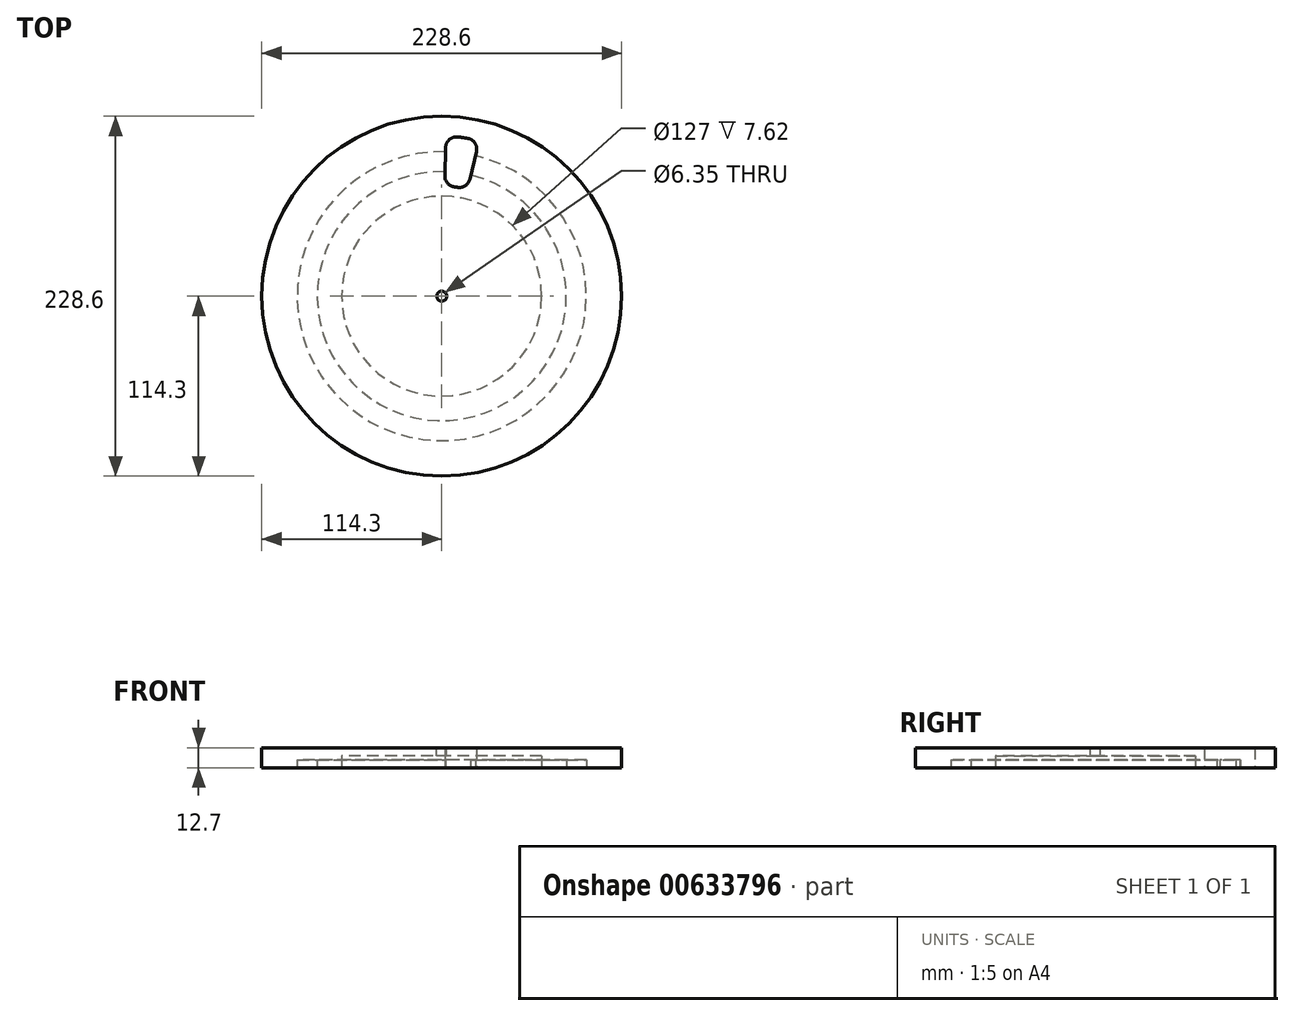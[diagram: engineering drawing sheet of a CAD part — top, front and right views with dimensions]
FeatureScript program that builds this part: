
annotation { "Feature Type Name" : "Feature", "Feature Type Description" : "" }
export const myFeature = defineFeature(function(context is Context, id is Id, definition is map)
    precondition{}
    {
        {
            var Q0;
            Q0=qCreatedBy(makeId("Top.planeOp"),FACE);
            var sketch = newSketch(context, id + "F0", { "sketchPlane" : qUnion([Q0])});
            skCircle(sketch, "E0", {"center": v(0, 0) * mm, "radius": 114.3 * mm});
            skSolve(sketch);
        }
        {
            var Q0;
            Q0 = qSketchRegion(id + "F0", true);
            extrude(context, id + "F1", {"entities" : qUnion([Q0]), "depth" : 12.7 * mm, "offsetDistance" : 25.4 * mm});
        }
        {
            var Q0;
            Q0=qCreatedBy(makeId("Top.planeOp"),FACE);
            var sketch = newSketch(context, id + "F2", { "sketchPlane" : qUnion([Q0])});
            skCircle(sketch, "E1", {"center": v(0, 0) * mm, "radius": 63.5 * mm});
            skSolve(sketch);
        }
        {
            var Q0;
            Q0 = qSketchRegion(id + "F2", true);
            var Q1;
            Q1=makeQuery(id+"F1.opExtrude","CAP_FACE",FACE,{"disambiguationData":[OSD([sQuery(id+"F0.wireOp",EDGE,"E0")])],"isStart":false});
            extrude(context, id + "F3", {"entities" : qUnion([Q0]), "operationType" : NewBodyOperationType.REMOVE, "endBound" : BoundingType.UP_TO_SURFACE, "depth" : 20.32 * mm, "endBoundEntityFace" : qUnion([Q1]), "hasOffset" : true, "offsetDistance" : 5.08 * mm});
        }
        {
            var Q0;
            Q0=makeQuery(id+"F1.opExtrude","CAP_FACE",FACE,{"disambiguationData":[OSD([sQuery(id+"F0.wireOp",EDGE,"E0")])],"isStart":true});
            var sketch = newSketch(context, id + "F4", { "sketchPlane" : qUnion([Q0])});
            skLineSegment(sketch, "E2", {"start": v(0, 0) * mm, "end": v(0, -114.3) * mm, "construction": true});
            skLineSegment(sketch, "E3", {"start": v(0, 0) * mm, "end": v(3, -114.26) * mm, "construction": true});
            skLineSegment(sketch, "E4", {"start": v(0, 0) * mm, "end": v(29.58, -110.4) * mm, "construction": true});
            skLineSegment(sketch, "E5", {"start": v(0, 0) * mm, "end": v(26.68, -111.14) * mm, "construction": true});
            skArc(sketch, "E6", {"start": v(10, -101.1) * mm, "mid": v(13.26, -100.73) * mm, "end": v(16.5, -100.25) * mm});
            skArc(sketch, "E7", {"start": v(8.06, -69.38) * mm, "mid": v(9.12, -69.25) * mm, "end": v(10.17, -69.1) * mm});
            skLineSegment(sketch, "E8", {"start": v(17.84, -74.29) * mm, "end": v(22.06, -91.88) * mm});
            skLineSegment(sketch, "E9", {"start": v(2, -76.37) * mm, "end": v(2.47, -94.46) * mm});
            skPoint(sketch, "E10.visualSharp", {"position": v(1.83, -69.83) * mm});
            skArc(sketch, "E10.filletArc", {"start": v(8.06, -69.38) * mm, "mid": v(3.67, -71.7) * mm, "end": v(2, -76.37) * mm});
            skPoint(sketch, "E11.visualSharp", {"position": v(16.3, -67.92) * mm});
            skArc(sketch, "E11.filletArc", {"start": v(17.84, -74.29) * mm, "mid": v(15, -70.2) * mm, "end": v(10.17, -69.1) * mm});
            skPoint(sketch, "E12.visualSharp", {"position": v(23.72, -98.8) * mm});
            skArc(sketch, "E12.filletArc", {"start": v(16.5, -100.25) * mm, "mid": v(21.1, -97.28) * mm, "end": v(22.06, -91.88) * mm});
            skPoint(sketch, "E13.visualSharp", {"position": v(2.66, -101.57) * mm});
            skArc(sketch, "E13.filletArc", {"start": v(2.47, -94.46) * mm, "mid": v(4.8, -99.42) * mm, "end": v(10, -101.1) * mm});
            skSolve(sketch);
        }
        {
            var Q0;
            Q0 = qSketchRegion(id + "F4", true);
            extrude(context, id + "F5", {"entities" : qUnion([Q0]), "operationType" : NewBodyOperationType.REMOVE, "endBound" : BoundingType.THROUGH_ALL, "oppositeDirection" : true, "depth" : 25.4 * mm, "offsetDistance" : 25.4 * mm});
        }
        {
            var Q0;
            Q0=makeQuery(id+"F1.opExtrude","CAP_FACE",FACE,{"disambiguationData":[OSD([sQuery(id+"F0.wireOp",EDGE,"E0")])],"isStart":false});
            var sketch = newSketch(context, id + "F6", { "sketchPlane" : qUnion([Q0])});
            skCircle(sketch, "E14", {"center": v(0, 0) * mm, "radius": 3.18 * mm});
            skSolve(sketch);
        }
        {
            var Q0;
            Q0 = qSketchRegion(id + "F6", true);
            extrude(context, id + "F7", {"entities" : qUnion([Q0]), "operationType" : NewBodyOperationType.REMOVE, "endBound" : BoundingType.THROUGH_ALL, "oppositeDirection" : true, "depth" : 25.4 * mm, "offsetDistance" : 25.4 * mm});
        }
        {
            var Q0;
            Q0=makeQuery(id+"F1.opExtrude","CAP_FACE",FACE,{"disambiguationData":[OSD([sQuery(id+"F0.wireOp",EDGE,"E0")])],"isStart":true});
            var sketch = newSketch(context, id + "F8", { "sketchPlane" : qUnion([Q0])});
            skCircle(sketch, "E15", {"center": v(0, 0) * mm, "radius": 79.1 * mm});
            skCircle(sketch, "E16", {"center": v(0, 0) * mm, "radius": 85.45 * mm, "construction": true});
            skCircle(sketch, "E17", {"center": v(0, 0) * mm, "radius": 91.8 * mm});
            skSolve(sketch);
        }
        {
            var Q0;
            Q0 = qSketchRegion(id + "F8", true);
            extrude(context, id + "F9", {"entities" : qUnion([Q0]), "operationType" : NewBodyOperationType.REMOVE, "oppositeDirection" : true, "depth" : 5.08 * mm, "offsetDistance" : 25.4 * mm});
        }
    });
